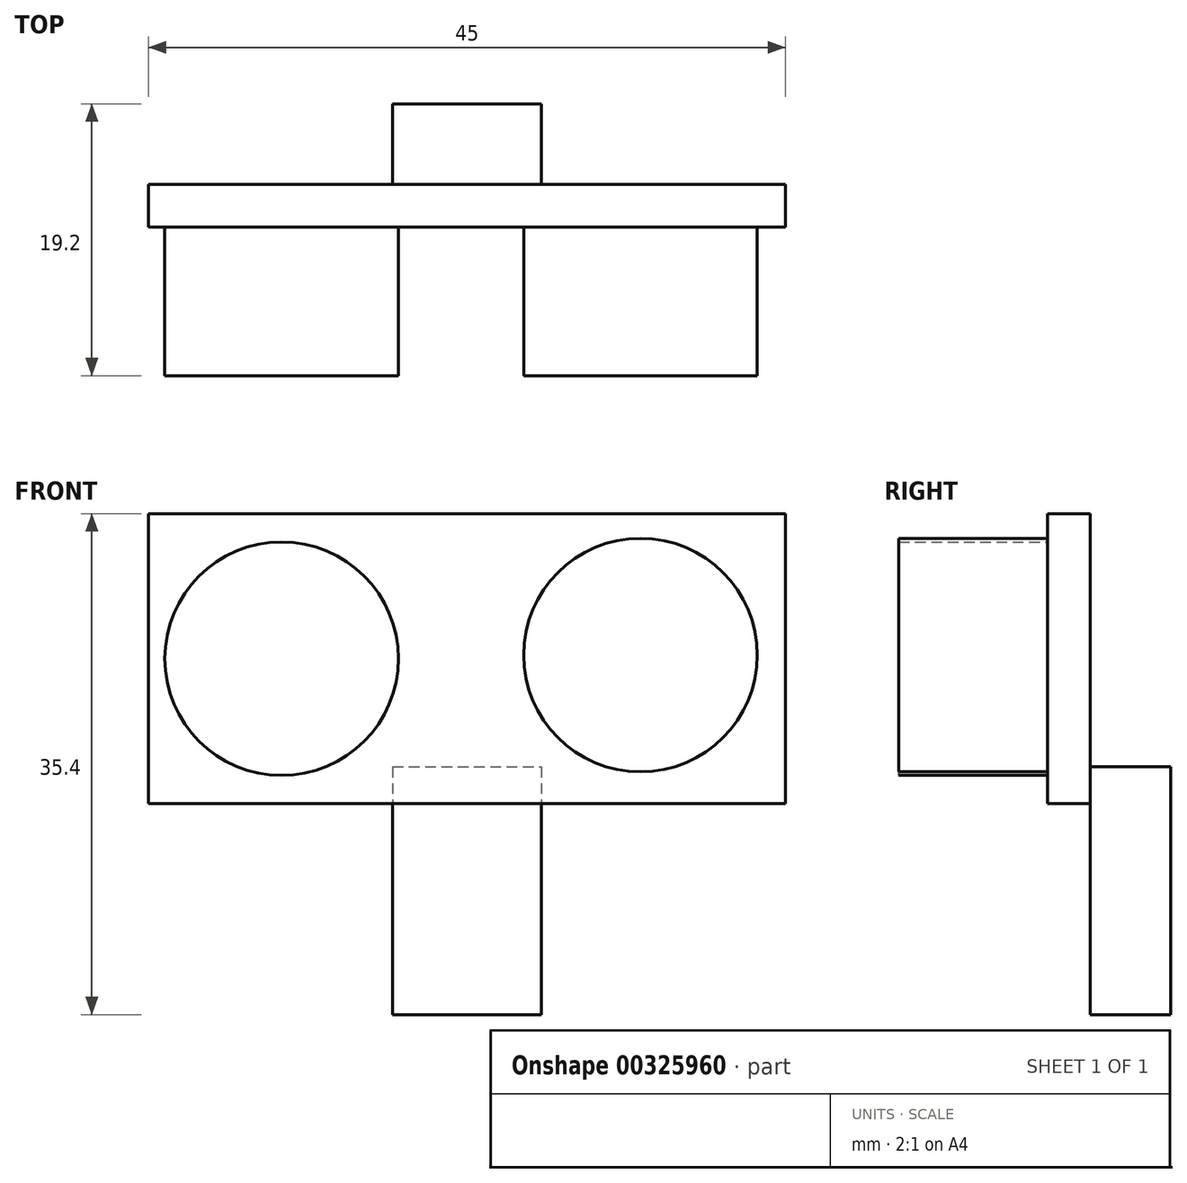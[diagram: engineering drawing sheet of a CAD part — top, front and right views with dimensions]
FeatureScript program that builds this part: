
annotation { "Feature Type Name" : "Feature", "Feature Type Description" : "" }
export const myFeature = defineFeature(function(context is Context, id is Id, definition is map)
    precondition{}
    {
        {
            var Q0;
            Q0=qCreatedBy(makeId("Front.planeOp"),FACE);
            var sketch = newSketch(context, id + "F0", { "sketchPlane" : qUnion([Q0])});
            skLineSegment(sketch, "E0.bottom", {"start": v(22.5, 10.25) * mm, "end": v(-22.5, 10.25) * mm});
            skLineSegment(sketch, "E0.top", {"start": v(22.5, -10.25) * mm, "end": v(-22.5, -10.25) * mm});
            skLineSegment(sketch, "E0.left", {"start": v(22.5, 10.25) * mm, "end": v(22.5, -10.25) * mm});
            skLineSegment(sketch, "E0.right", {"start": v(-22.5, 10.25) * mm, "end": v(-22.5, -10.25) * mm});
            skPoint(sketch, "E0.middle", {"position": v(0, 0) * mm});
            skLineSegment(sketch, "E1.bottom", {"start": v(-5.25, -7.65) * mm, "end": v(5.25, -7.65) * mm});
            skLineSegment(sketch, "E1.top", {"start": v(-5.25, -25.15) * mm, "end": v(5.25, -25.15) * mm});
            skLineSegment(sketch, "E1.left", {"start": v(-5.25, -7.65) * mm, "end": v(-5.25, -25.15) * mm});
            skLineSegment(sketch, "E1.right", {"start": v(5.25, -7.65) * mm, "end": v(5.25, -25.15) * mm});
            skPoint(sketch, "E1.middle", {"position": v(0, -16.4) * mm});
            skLineSegment(sketch, "E2", {"start": v(0, 0) * mm, "end": v(0, -7.65) * mm, "construction": true});
            skCircle(sketch, "E3", {"center": v(12.25, 0.25) * mm, "radius": 8.25 * mm});
            skCircle(sketch, "E4", {"center": v(-13.1, 0) * mm, "radius": 8.25 * mm});
            skSolve(sketch);
        }
        {
            var Q0;
            Q0=makeQuery(id+"F0.imprint","IMPRINT",FACE,{"disambiguationData":[TD([[makeQuery(id+"F0.imprint","IMPRINT",EDGE,{"derivedFrom":sQuery(id+"F0.wireOp",EDGE,"E0.bottom")}),1.0]])]});
            var Q1;
            {var subQ5=sQuery(id+"F0.wireOp",EDGE,"E1.bottom");Q1=makeQuery(id+"F0.imprint","IMPRINT",FACE,{"disambiguationData":[TD([[makeQuery(id+"F0.imprint","IMPRINT",EDGE,{"derivedFrom":subQ5}),-1.0]])]});}
            var Q2;
            Q2=makeQuery(id+"F0.imprint","IMPRINT",FACE,{"disambiguationData":[TD([[makeQuery(id+"F0.imprint","IMPRINT",EDGE,{"derivedFrom":sQuery(id+"F0.wireOp",EDGE,"E4")}),1.0]])]});
            var Q3;
            Q3=makeQuery(id+"F0.imprint","IMPRINT",FACE,{"disambiguationData":[TD([[makeQuery(id+"F0.imprint","IMPRINT",EDGE,{"derivedFrom":sQuery(id+"F0.wireOp",EDGE,"E3")}),1.0]])]});
            extrude(context, id + "F1", {"entities" : qUnion([Q0, Q1, Q2, Q3]), "depth" : 3 * mm});
        }
        {
            var Q0;
            {var subQ5=sQuery(id+"F0.wireOp",EDGE,"E1.bottom");Q0=makeQuery(id+"F0.imprint","IMPRINT",FACE,{"disambiguationData":[TD([[makeQuery(id+"F0.imprint","IMPRINT",EDGE,{"derivedFrom":subQ5}),-1.0]])]});}
            var Q1;
            {var subQ5=sQuery(id+"F0.wireOp",EDGE,"E1.top");Q1=makeQuery(id+"F0.imprint","IMPRINT",FACE,{"disambiguationData":[TD([[makeQuery(id+"F0.imprint","IMPRINT",EDGE,{"derivedFrom":subQ5}),1.0]])]});}
            extrude(context, id + "F2", {"entities" : qUnion([Q0, Q1]), "operationType" : NewBodyOperationType.ADD, "oppositeDirection" : true, "depth" : 5.7 * mm});
        }
        {
            var Q0;
            Q0=makeQuery(id+"F0.imprint","IMPRINT",FACE,{"disambiguationData":[TD([[makeQuery(id+"F0.imprint","IMPRINT",EDGE,{"derivedFrom":sQuery(id+"F0.wireOp",EDGE,"E4")}),1.0]])]});
            var Q1;
            Q1=makeQuery(id+"F0.imprint","IMPRINT",FACE,{"disambiguationData":[TD([[makeQuery(id+"F0.imprint","IMPRINT",EDGE,{"derivedFrom":sQuery(id+"F0.wireOp",EDGE,"E3")}),1.0]])]});
            extrude(context, id + "F3", {"entities" : qUnion([Q0, Q1]), "operationType" : NewBodyOperationType.ADD, "depth" : 13.5 * mm});
        }
    });
